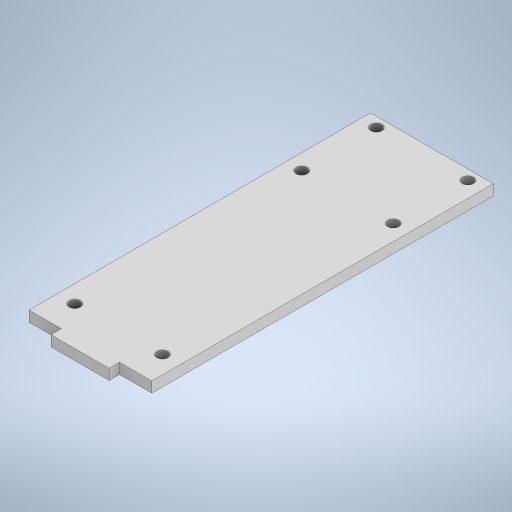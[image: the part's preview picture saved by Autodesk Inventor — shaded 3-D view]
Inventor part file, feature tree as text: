
AUTODESK INVENTOR PART (.ipt)
format: ipt  version: 2023 (Build 270158000, 158)  size: 243,712 bytes
history: native  units: mm
features: sketch x2, other x1, extrude x1, mirror x1, hole x1
ambient origin geometry x8: Origin, YZ Plane, XZ Plane, XY Plane, X Axis, Y Axis, Z Axis, Center Point
bodies: Body1 (feature_tree)
feature tree (6):
  other  "Твердое тело1"
  extrude  "Выдавливание1"  Depth=17.45mm
  mirror  "Зеркальное отражение1"
  hole  "Отверстие1"  [1 undecoded]
  sketch  "Эскиз1"
  sketch  "Эскиз2"
note: 1 required parameter value undecoded (feature->parameter linkage not recoverable at this tier; creation-order binding heuristic only, values carry confidence <= 0.55)
